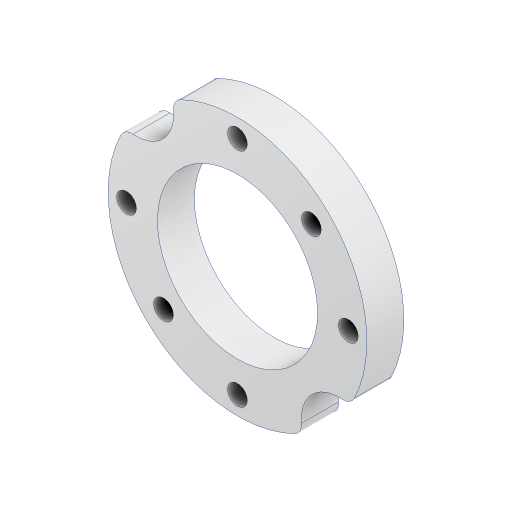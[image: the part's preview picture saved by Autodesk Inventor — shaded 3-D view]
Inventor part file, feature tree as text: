
AUTODESK INVENTOR PART (.ipt)
format: ipt  version: 2023 (Build 270158000, 158)  size: 283,136 bytes
history: native  units: mm
features: other x5, extrude x2, sketch x2, fillet x1, reference x1, projected_geometry x1
ambient origin geometry x8: Origin, YZ Plane, XZ Plane, XY Plane, X Axis, Y Axis, Z Axis, Center Point
bodies: Body1 (feature_tree)
feature tree (12):
  other  "솔리드1"
  other  "작업 평면1"
  extrude  "돌출1"  Depth=42.0mm
  fillet  "모깎기1"  Radius=5.0mm
  extrude  "돌출2"  Depth=2.0mm
  sketch  "스케치1"
  reference  "참조1"
  sketch  "스케치2"
  projected_geometry  "투영된 루프1"
  other  "<userpath>\Desktop\2022 manipulator (국방로봇)\JWM.iam"
  other  "JWM.iam"
  other  "기어2:6"
